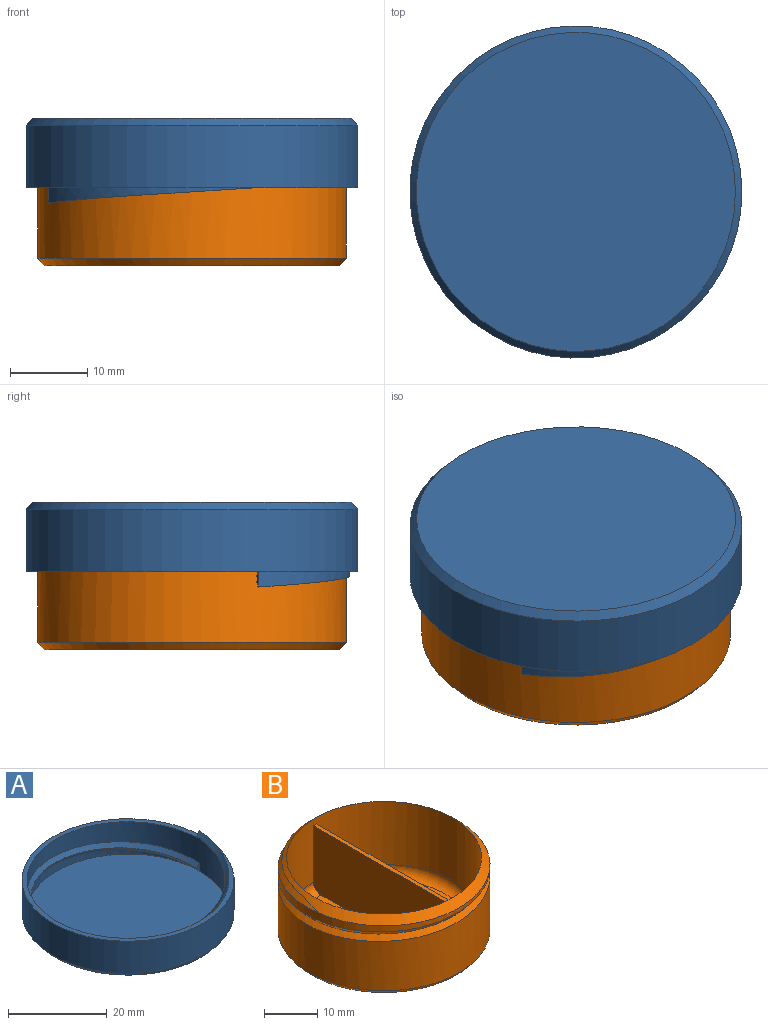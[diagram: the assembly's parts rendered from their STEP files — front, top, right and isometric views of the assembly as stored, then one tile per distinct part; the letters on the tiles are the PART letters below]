
ASSEMBLY  parts=2 mates=1
PART A: 12 faces, bbox 43x43x11 mm
  f0: cylinder r=21.5mm len=43mm, axis (0,0,-1), area 1080.7mm2, adj f2,f3
  f1: plane 41.32x41.32mm, normal (0,0,-1), area 1341.1mm2, adj f2
  f2: cone r=21.5mm half-angle=40deg, axis (0,0,1), area 172.9mm2, adj f0,f1
  f3: plane 43x43mm, normal (0,0,1), area 138.4mm2, adj f0,f8,f11
  f4: plane 40.9x40.9mm, normal (0,0,1), area 1313.8mm2, adj f11
  f5: plane 2x0.8mm, normal (0,-1,0), area 0.8mm2, adj f6,f9,f10,f11
  f6: cylinder r=19.65mm len=39.3mm, axis (0,0,1), area 11.5mm2, adj f5,f7,f9,f10
  f7: plane 2x0.8mm, normal (0,1,0), area 0.8mm2, adj f6,f8,f9,f10
  f8: cylinder r=20.45mm len=20.45mm, axis (0,0,1), area 32.1mm2, adj f3,f7,f9
  f9: bspline ~40.9x40.9mm, area 156.9mm2, adj f5,f6,f7,f8,f11
  f10: bspline ~40.9x40.9mm, area 157mm2, adj f5,f6,f7,f11
  f11: cylinder r=20.45mm len=40.9mm, axis (0,0,1), area 803.1mm2, adj f3,f4,f5,f9,f10
PART B: 20 faces, bbox 40x46.2x18.1 mm
  f0: cylinder r=19.1mm len=38.2mm, axis (0,0,1), area 3.1mm2, adj f9,f10,f14,f18
  f1: plane 32.79x15.98mm, normal (0,0,1), area 408.5mm2, adj f4,f15
  f2: plane 32.79x15.98mm, normal (0,0,1), area 408.5mm2, adj f3,f16
  f3: torus R=16.4mm, axis (0,0,1), area 171.7mm2, adj f2,f5,f16
  f4: torus R=16.4mm, axis (0,0,1), area 171.7mm2, adj f1,f5,f15
  f5: cylinder r=18.4mm len=36.8mm, axis (0,0,1), area 1665.7mm2, adj f3,f4,f14,f15,f16,f17
  f6: cylinder r=20mm len=40mm, axis (0,0,-1), area 1370.9mm2, adj f7,f10,f12,f13
  f7: cylinder r=20mm len=40mm, axis (0,0,-1), area 170.9mm2, adj f6,f9,f10,f14
  f8: cylinder r=19.1mm len=38.2mm, axis (0,0,1), area 3.2mm2, adj f9,f10,f12,f19
  f9: bspline ~46.19x40mm, area 210.3mm2, adj f0,f7,f8,f12,f14,f18,f19
  f10: bspline ~46.19x40mm, area 258.3mm2, adj f0,f6,f7,f8,f12,f14,f18,f19
  f11: plane 38.32x38.32mm, normal (0,0,-1), area 1153.4mm2, adj f13
  f12: plane 2.18x0.9mm, normal (0,1,0), area 1mm2, adj f6,f8,f9,f10
  f13: cone r=20mm half-angle=40deg, axis (0,0,1), area 160.6mm2, adj f6,f11
  f14: cone r=20mm half-angle=45deg, axis (0,0,-1), area 229.1mm2, adj f0,f5,f7,f9,f10
  f15: plane 36.82x15.02mm, normal (-1,0,0), area 550.1mm2, adj f1,f4,f5,f17
  f16: plane 36.82x15.02mm, normal (1,0,0), area 550.1mm2, adj f2,f3,f5,f17
  f17: plane 36.8x0.85mm, normal (0,0,1), area 31.3mm2, adj f5,f15,f16
  f18: plane 0.15x0.05mm, normal (0.87,-0.49,0), area 0mm2, adj f0,f9,f10,f19
  f19: plane 0.15x0.05mm, normal (-0.87,-0.49,0), area 0mm2, adj f8,f9,f10,f18
PLACE A rot(axis=(0.21,-0.98,0),180deg) t=(-7.25,-0.74,18.05)mm
PLACE B t=(-7.25,-0.74,-1.09)mm fixed
MATE cylindrical A.f6 <-> B.f3  axis (0,0,-1) through (-7.25,-0.74,17.05)mm
